# Revit family: Door-Slider-Fleetwood-3050-OX
name_source: partatom
category: Doors
revit_build: Autodesk Revit Architecture 2013 (Build: 20120221_2030(x64)
units: mm (PartAtom-declared; Revit-internal decimal feet)

## types (4) — shared parameters
1"_Hidden_Sill = No
1.5"_Hidden_Sill = Yes
Analytic Construction = <None>
Centerline_1 = 0' - 0"
Centerline_Calc = 4' - 0"
Configuration = OX
Equal_Centerlines = Yes
Exterior Wrap Overhang = 0' - 0 1/2"
Frame_&_Panel = Aluminum, Anodized Clear
Function = Exterior
Glazing = Glass
Hardware = Stainless Steel, Brushed
Height = 8' - 0"
Interior Wrap Overhang = 0' - 0 1/2"
Manufacturer = Fleetwood Windows and Doors
Model = 3050
Number_Of_Tracks = 2
Panel_1 = 4' - 0 9/32"
Panel_2 = 4' - 0 1/16"
Rough Height = 8' - 0 1/4"
Rough Width = 8' - 0 1/2"
Sill_Height = 0' - 1 1/2"
Thickness = 0' - 3 13/16"
URL = www.fleetwoodusa.com
Wall Closure = By host
Width = 8' - 0"

## per-type parameters (varying)
| type | Actuator_Height | Panel_1_Configuration | Panel_2_Configuration |
| Archetype Hardware_Archetype Fixed Stile | 4' - 5 3/4" | 3050_Panel : Fixed Panel Archetype Stile | 3050_Panel : Active Lead Panel Right Archetype |
| Archetype Narrow Hardware_Archetype Narrow Fixed Stile | 3' - 10" | 3050_Panel : Fixed Panel Archetype Narrow Stile | 3050_Panel : Active Lead Panel Right Archetype Narrow |
| Archetype Narrow Hardware_Archetype Fixed Stile | 3' - 10" | 3050_Panel : Fixed Panel Archetype Stile | 3050_Panel : Active Lead Panel Right Archetype Narrow |
| Archetype Hardware_Archetype Narrow Fixed Stile | 4' - 5 3/4" | 3050_Panel : Fixed Panel Archetype Narrow Stile | 3050_Panel : Active Lead Panel Right Archetype |

## geometry (parser evidence)
native form markers: Blend x14, Sweep x15
no freeform markers — native parametric forms only
